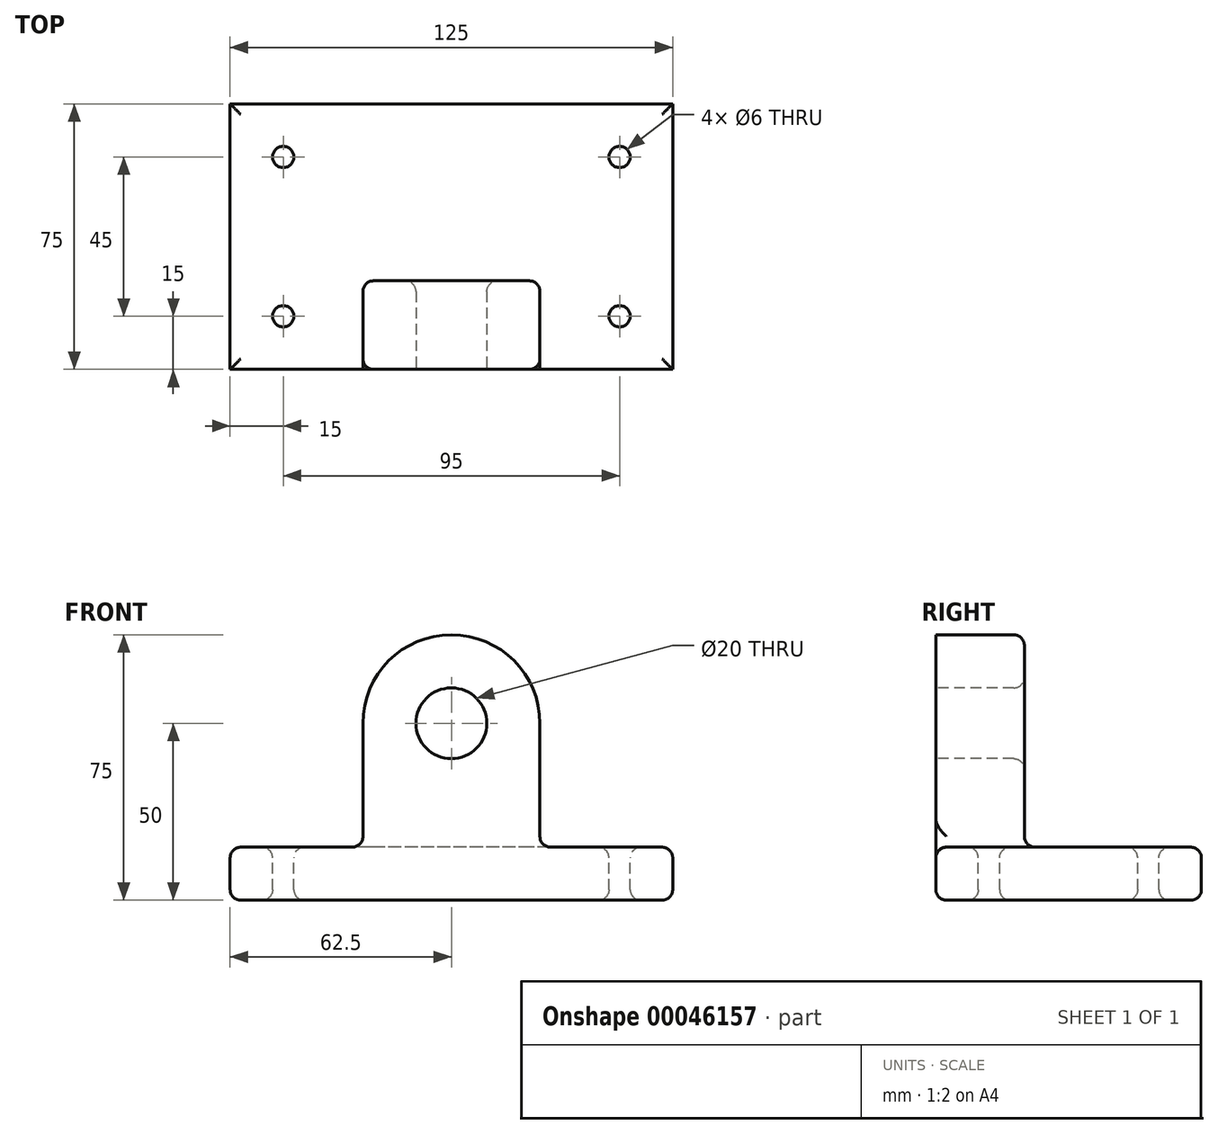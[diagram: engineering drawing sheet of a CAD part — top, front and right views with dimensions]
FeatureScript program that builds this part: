
annotation { "Feature Type Name" : "Feature", "Feature Type Description" : "" }
export const myFeature = defineFeature(function(context is Context, id is Id, definition is map)
    precondition{}
    {
        {
            var Q0;
            Q0=qCreatedBy(makeId("Top.planeOp"),FACE);
            var sketch = newSketch(context, id + "F0", { "sketchPlane" : qUnion([Q0])});
            skLineSegment(sketch, "E0.rect.bottom", {"start": v(62.5, 37.5) * mm, "end": v(-62.5, 37.5) * mm});
            skLineSegment(sketch, "E0.rect.top", {"start": v(62.5, -37.5) * mm, "end": v(-62.5, -37.5) * mm});
            skLineSegment(sketch, "E0.rect.left", {"start": v(62.5, 37.5) * mm, "end": v(62.5, -37.5) * mm});
            skLineSegment(sketch, "E0.rect.right", {"start": v(-62.5, 37.5) * mm, "end": v(-62.5, -37.5) * mm});
            skPoint(sketch, "E0.rect.middle", {"position": v(0, 0) * mm});
            skSolve(sketch);
        }
        {
            var Q0;
            Q0=makeQuery(id+"F0.imprint","IMPRINT",FACE,{"disambiguationData":[TD([[makeQuery(id+"F0.imprint","IMPRINT",EDGE,{"derivedFrom":sQuery(id+"F0.wireOp",EDGE,"E0.rect.bottom")}),1.0]])]});
            extrude(context, id + "F1", {"entities" : qUnion([Q0]), "depth" : 15 * mm});
        }
        {
            var Q0;
            Q0=makeQuery(id+"F1.opExtrude","SWEPT_FACE",FACE,{"disambiguationData":[OSD([sQuery(id+"F0.wireOp",EDGE,"E0.rect.top")])]});
            var sketch = newSketch(context, id + "F2", { "sketchPlane" : qUnion([Q0])});
            skLineSegment(sketch, "E1", {"start": v(0, 0) * mm, "end": v(0, 50) * mm, "construction": true});
            skLineSegment(sketch, "E2.rect.bottom", {"start": v(25, 0) * mm, "end": v(-25, 0) * mm});
            skLineSegment(sketch, "E2.rect.top", {"start": v(25, 50) * mm, "end": v(-25, 50) * mm});
            skLineSegment(sketch, "E2.rect.left", {"start": v(25, 0) * mm, "end": v(25, 50) * mm});
            skLineSegment(sketch, "E2.rect.right", {"start": v(-25, 0) * mm, "end": v(-25, 50) * mm});
            skPoint(sketch, "E2.rect.middle", {"position": v(0, 25) * mm});
            skCircle(sketch, "E3", {"center": v(0, 50) * mm, "radius": 25 * mm});
            skCircle(sketch, "E4", {"center": v(0, 50) * mm, "radius": 10 * mm});
            skSolve(sketch);
        }
        {
            var Q0;
            {var subQ0=sQuery(id+"F2.wireOp",EDGE,"E4");var subQ1=sQuery(id+"F2.wireOp",EDGE,"E2.rect.top");var subQ3=makeQuery(id+"F2.imprint","INTERSECT",VERTEX,{"disambiguationData":[OD(0.0)],"derivedFrom":[subQ1,subQ0]});Q0=makeQuery(id+"F2.imprint","IMPRINT",FACE,{"disambiguationData":[TD([[makeQuery(id+"F2.imprint","IMPRINT",EDGE,{"disambiguationData":[TD([[subQ3,-1.0]])],"derivedFrom":subQ0}),-1.0]])]});}
            var Q1;
            {var subQ0=makeQuery(id+"F1.opExtrude","CAP_EDGE",EDGE,{"disambiguationData":[OSD([sQuery(id+"F0.wireOp",EDGE,"E0.rect.top")])],"isStart":false});var subQ3=sQuery(id+"F2.wireOp",EDGE,"E2.rect.left");var subQ4=makeQuery(id+"F2.imprint","INTERSECT",VERTEX,{"derivedFrom":[subQ0,subQ3]});Q1=makeQuery(id+"F2.imprint","IMPRINT",FACE,{"disambiguationData":[TD([[makeQuery(id+"F2.imprint","IMPRINT",EDGE,{"disambiguationData":[TD([[subQ4,-1.0]])],"derivedFrom":subQ0}),-1.0]])]});}
            var Q2;
            {var subQ0=sQuery(id+"F2.wireOp",EDGE,"E4");var subQ1=sQuery(id+"F2.wireOp",EDGE,"E2.rect.top");var subQ3=makeQuery(id+"F2.imprint","INTERSECT",VERTEX,{"disambiguationData":[OD(0.0)],"derivedFrom":[subQ1,subQ0]});Q2=makeQuery(id+"F2.imprint","IMPRINT",FACE,{"disambiguationData":[TD([[makeQuery(id+"F2.imprint","IMPRINT",EDGE,{"disambiguationData":[TD([[subQ3,1.0]])],"derivedFrom":subQ0}),-1.0]])]});}
            extrude(context, id + "F3", {"entities" : qUnion([Q0, Q1, Q2]), "operationType" : NewBodyOperationType.ADD, "oppositeDirection" : true, "depth" : 25 * mm});
        }
        {
            var Q0;
            Q0=makeQuery(id+"F1.opExtrude","CAP_FACE",FACE,{"disambiguationData":[OSD([sQuery(id+"F0.wireOp",EDGE,"E0.rect.bottom"),sQuery(id+"F0.wireOp",EDGE,"E0.rect.top"),sQuery(id+"F0.wireOp",EDGE,"E0.rect.left"),sQuery(id+"F0.wireOp",EDGE,"E0.rect.right")])],"isStart":false});
            var sketch = newSketch(context, id + "F4", { "sketchPlane" : qUnion([Q0])});
            skLineSegment(sketch, "E5.rect.bottom", {"start": v(47.5, 22.5) * mm, "end": v(-47.5, 22.5) * mm, "construction": true});
            skLineSegment(sketch, "E5.rect.top", {"start": v(47.5, -22.5) * mm, "end": v(-47.5, -22.5) * mm, "construction": true});
            skLineSegment(sketch, "E5.rect.left", {"start": v(47.5, 22.5) * mm, "end": v(47.5, -22.5) * mm, "construction": true});
            skLineSegment(sketch, "E5.rect.right", {"start": v(-47.5, 22.5) * mm, "end": v(-47.5, -22.5) * mm, "construction": true});
            skPoint(sketch, "E5.rect.middle", {"position": v(0, 0) * mm});
            skCircle(sketch, "E6", {"center": v(-47.5, 22.5) * mm, "radius": 3 * mm});
            skCircle(sketch, "E7", {"center": v(47.5, 22.5) * mm, "radius": 3 * mm});
            skCircle(sketch, "E8", {"center": v(47.5, -22.5) * mm, "radius": 3 * mm});
            skCircle(sketch, "E9", {"center": v(-47.5, -22.5) * mm, "radius": 3 * mm});
            skSolve(sketch);
        }
        {
            var Q0;
            Q0=makeQuery(id+"F4.imprint","IMPRINT",FACE,{"disambiguationData":[TD([[makeQuery(id+"F4.imprint","IMPRINT",EDGE,{"derivedFrom":sQuery(id+"F4.wireOp",EDGE,"E9")}),1.0]])]});
            var Q1;
            Q1=makeQuery(id+"F4.imprint","IMPRINT",FACE,{"disambiguationData":[TD([[makeQuery(id+"F4.imprint","IMPRINT",EDGE,{"derivedFrom":sQuery(id+"F4.wireOp",EDGE,"E7")}),1.0]])]});
            var Q2;
            Q2=makeQuery(id+"F4.imprint","IMPRINT",FACE,{"disambiguationData":[TD([[makeQuery(id+"F4.imprint","IMPRINT",EDGE,{"derivedFrom":sQuery(id+"F4.wireOp",EDGE,"E8")}),1.0]])]});
            var Q3;
            Q3=makeQuery(id+"F4.imprint","IMPRINT",FACE,{"disambiguationData":[TD([[makeQuery(id+"F4.imprint","IMPRINT",EDGE,{"derivedFrom":sQuery(id+"F4.wireOp",EDGE,"E6")}),1.0]])]});
            extrude(context, id + "F5", {"entities" : qUnion([Q0, Q1, Q2, Q3]), "operationType" : NewBodyOperationType.REMOVE, "endBound" : BoundingType.UP_TO_NEXT, "oppositeDirection" : true, "depth" : 25 * mm});
        }
        {
            var Q0;
            Q0=makeQuery(id+"F1.opExtrude","CAP_FACE",FACE,{"disambiguationData":[OSD([sQuery(id+"F0.wireOp",EDGE,"E0.rect.bottom"),sQuery(id+"F0.wireOp",EDGE,"E0.rect.top"),sQuery(id+"F0.wireOp",EDGE,"E0.rect.left"),sQuery(id+"F0.wireOp",EDGE,"E0.rect.right")])],"isStart":false});
            var Q1;
            Q1=makeQuery(id+"F3.opExtrude","CAP_FACE",FACE,{"disambiguationData":[OSD([sQuery(id+"F0.wireOp",EDGE,"E0.rect.top"),sQuery(id+"F2.wireOp",EDGE,"E2.rect.left"),sQuery(id+"F2.wireOp",EDGE,"E2.rect.right"),sQuery(id+"F2.wireOp",EDGE,"E3"),sQuery(id+"F2.wireOp",EDGE,"E4")])],"isStart":false});
            var Q2;
            Q2=makeQuery(id+"F1.opExtrude","CAP_FACE",FACE,{"disambiguationData":[OSD([sQuery(id+"F0.wireOp",EDGE,"E0.rect.bottom"),sQuery(id+"F0.wireOp",EDGE,"E0.rect.top"),sQuery(id+"F0.wireOp",EDGE,"E0.rect.left"),sQuery(id+"F0.wireOp",EDGE,"E0.rect.right")])],"isStart":true});
            fillet(context, id + "F6", {"entities" : qUnion([Q0, Q1, Q2]), "radius" : 3 * mm, "tangentPropagation" : true, "allowEdgeOverflow" : false});
        }
    });
